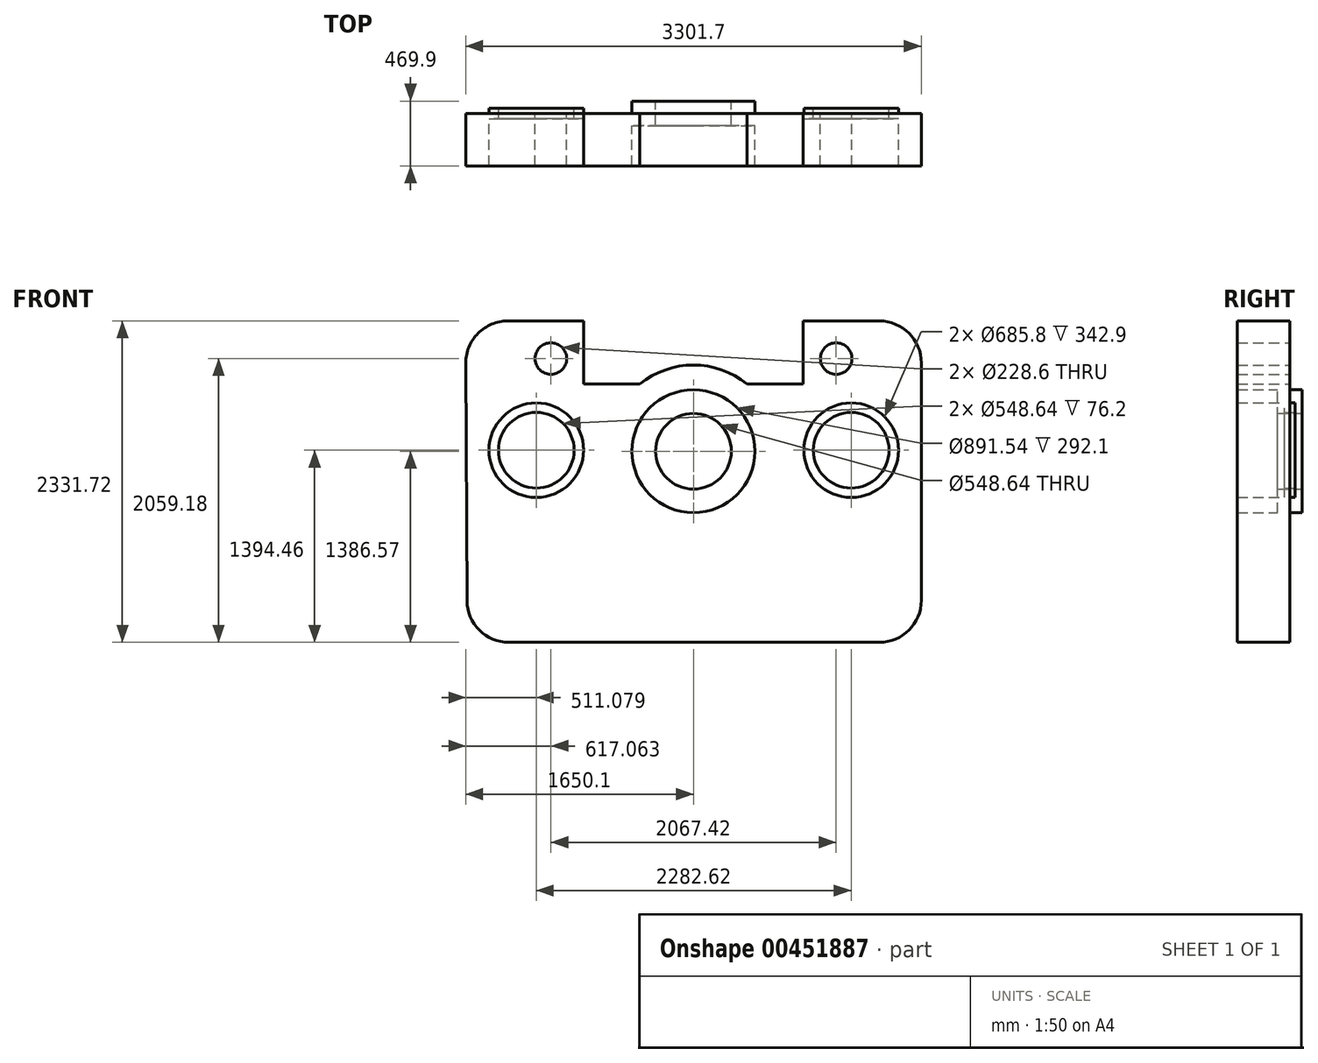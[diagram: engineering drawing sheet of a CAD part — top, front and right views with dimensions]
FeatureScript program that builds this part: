
annotation { "Feature Type Name" : "Feature", "Feature Type Description" : "" }
export const myFeature = defineFeature(function(context is Context, id is Id, definition is map)
    precondition{}
    {
        {
            var Q0;
            Q0=qCreatedBy(makeId("Front.planeOp"),FACE);
            var sketch = newSketch(context, id + "F0", { "sketchPlane" : qUnion([Q0])});
            skLineSegment(sketch, "E0", {"start": v(230.9, -60.48) * mm, "end": v(2914.61, -60.48) * mm});
            skLineSegment(sketch, "E1", {"start": v(3219.41, 244.32) * mm, "end": v(3219.41, 1966.44) * mm});
            skLineSegment(sketch, "E2", {"start": v(2914.61, 2271.24) * mm, "end": v(2362.16, 2271.24) * mm});
            skLineSegment(sketch, "E3", {"start": v(2362.16, 2271.24) * mm, "end": v(2362.16, 1814.04) * mm});
            skLineSegment(sketch, "E4", {"start": v(2362.16, 1814.04) * mm, "end": v(1955.76, 1814.04) * mm});
            skLineSegment(sketch, "E5", {"start": v(773.47, 1814.04) * mm, "end": v(773.47, 2271.24) * mm});
            skLineSegment(sketch, "E6", {"start": v(773.47, 2271.24) * mm, "end": v(222.5, 2271.24) * mm});
            skLineSegment(sketch, "E7", {"start": v(-82.29, 1964.95) * mm, "end": v(-73.9, 242.83) * mm});
            skPoint(sketch, "E8.visualSharp", {"position": v(-83.78, 2271.24) * mm});
            skArc(sketch, "E8.filletArc", {"start": v(222.5, 2271.24) * mm, "mid": v(6.46, 2181.44) * mm, "end": v(-82.29, 1964.95) * mm});
            skPoint(sketch, "E9.visualSharp", {"position": v(3219.41, 2271.24) * mm});
            skArc(sketch, "E9.filletArc", {"start": v(3219.41, 1966.44) * mm, "mid": v(3130.14, 2181.96) * mm, "end": v(2914.61, 2271.24) * mm});
            skArc(sketch, "E10", {"start": v(1955.76, 1814.04) * mm, "mid": v(1567.82, 1951.2) * mm, "end": v(1179.87, 1814.04) * mm});
            skLineSegment(sketch, "E11.trimOffspring", {"start": v(1179.87, 1814.04) * mm, "end": v(773.47, 1814.04) * mm});
            skPoint(sketch, "E12.visualSharp", {"position": v(-72.43, -60.48) * mm});
            skArc(sketch, "E12.filletArc", {"start": v(-73.9, 242.83) * mm, "mid": v(15.9, 28.27) * mm, "end": v(230.9, -60.48) * mm});
            skPoint(sketch, "E13.visualSharp", {"position": v(3219.41, -60.48) * mm});
            skArc(sketch, "E13.filletArc", {"start": v(2914.61, -60.48) * mm, "mid": v(3130.14, 28.8) * mm, "end": v(3219.41, 244.32) * mm});
            skCircle(sketch, "E14", {"center": v(1567.81, 1326.1) * mm, "radius": 445.77 * mm});
            skCircle(sketch, "E15", {"center": v(1567.81, 1326.1) * mm, "radius": 274.32 * mm});
            skCircle(sketch, "E16", {"center": v(428.79, 1333.98) * mm, "radius": 342.9 * mm});
            skCircle(sketch, "E17", {"center": v(428.79, 1333.98) * mm, "radius": 274.32 * mm});
            skCircle(sketch, "E18", {"center": v(2711.41, 1333.98) * mm, "radius": 342.9 * mm});
            skCircle(sketch, "E19", {"center": v(2711.41, 1333.98) * mm, "radius": 274.32 * mm});
            skCircle(sketch, "E20", {"center": v(534.77, 1998.7) * mm, "radius": 114.3 * mm});
            skCircle(sketch, "E21", {"center": v(2602.2, 1998.7) * mm, "radius": 114.3 * mm});
            skSolve(sketch);
        }
        {
            var Q0;
            Q0=makeQuery(id+"F0.imprint","IMPRINT",FACE,{"disambiguationData":[TD([[makeQuery(id+"F0.imprint","IMPRINT",EDGE,{"derivedFrom":sQuery(id+"F0.wireOp",EDGE,"E0")}),1.0]])]});
            extrude(context, id + "F1", {"entities" : qUnion([Q0]), "depth" : 381 * mm});
        }
        {
            var Q0;
            Q0=makeQuery(id+"F0.imprint","IMPRINT",FACE,{"disambiguationData":[TD([[makeQuery(id+"F0.imprint","IMPRINT",EDGE,{"derivedFrom":sQuery(id+"F0.wireOp",EDGE,"E14")}),1.0]])]});
            extrude(context, id + "F2", {"entities" : qUnion([Q0]), "operationType" : NewBodyOperationType.ADD, "depth" : 177.8 * mm, "symmetric" : true});
        }
        {
            var Q0;
            Q0=makeQuery(id+"F0.imprint","IMPRINT",FACE,{"disambiguationData":[TD([[makeQuery(id+"F0.imprint","IMPRINT",EDGE,{"derivedFrom":sQuery(id+"F0.wireOp",EDGE,"E18")}),1.0]])]});
            var Q1;
            Q1=makeQuery(id+"F0.imprint","IMPRINT",FACE,{"disambiguationData":[TD([[makeQuery(id+"F0.imprint","IMPRINT",EDGE,{"derivedFrom":sQuery(id+"F0.wireOp",EDGE,"E16")}),1.0]])]});
            extrude(context, id + "F3", {"entities" : qUnion([Q0, Q1]), "operationType" : NewBodyOperationType.ADD, "depth" : 76.2 * mm, "symmetric" : true});
        }
    });
